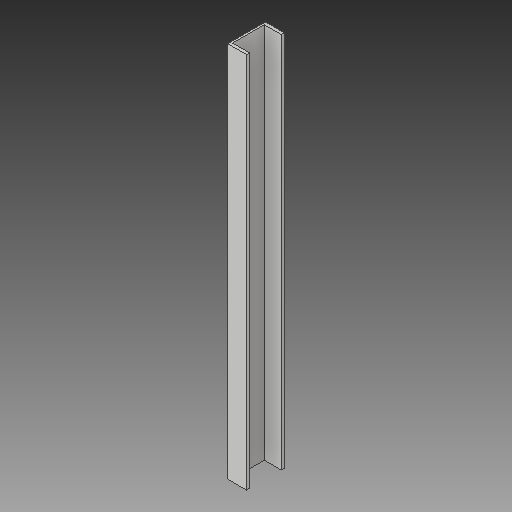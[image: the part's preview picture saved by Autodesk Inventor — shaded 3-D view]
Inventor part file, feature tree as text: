
AUTODESK INVENTOR PART (.ipt)
format: ipt  version: 2019 (Build 230136000, 136)  size: 90,624 bytes
history: native  units: in
note: dims shown in document units (in); Inventor stores cm internally (conversion verified against a paired STEP export)
features: other x3, sketch x1
ambient origin geometry x8: Origin, YZ Plane, XZ Plane, XY Plane, X Axis, Y Axis, Z Axis, Center Point
bodies: Solid1 (feature_tree)
feature tree (4):
  other  "Channel1_MIR.ipt"
  other  "Solid1::Channel1_MIR.ipt"
  other  "TaggingFeature1"
  sketch  "Sketch1"  dims[d0=0.3937in]
